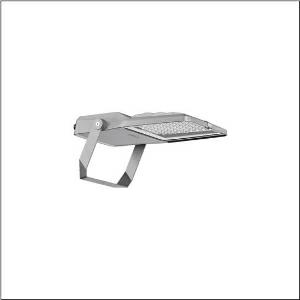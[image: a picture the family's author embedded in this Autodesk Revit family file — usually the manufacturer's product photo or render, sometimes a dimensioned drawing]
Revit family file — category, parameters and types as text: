
# Revit family: floodlight_fl_21_mini___pl64_5xa7776c4e1a_25dc
name_source: partatom
category: Lighting Fixtures
units: mm (PartAtom-declared; Revit-internal decimal feet)

## family parameters
Cut with Voids When Loaded = No
Host = Face
Light Source = No
Part Type = Normal
Room Calculation Point = No
Round Connector Dimension = Use Diameter
Shared = No

## types (1)
- --- (1 x LED, 12260 lm, 89 W, 4000K)
    Apparent Load = 89 VA
    CIE Flux Codes = 28 80 98 100 100
    Color Rendering = 70
    Color Temperature = 4000K
    Default Elevation = 1800 mm
    Description = Floodlight FL 21 mini, floodlight, primary light control with lens, of PMMA, primary optical cover: protective disc, of toughened safety glass, transparent, light distribution: PL64, light emission: direct distribution, installation type: surface-mounted, LED, High Power LED, rated luminous flux: 12.260lm, luminous efficacy: 138lm/W, light colour: 740, colour temperature: 4000K, control gear: D4iSmart Interface (Zhaga), control: overheat protection, constant luminous flux control, time-dependent luminous flux control, flexible luminous flux parameterisation, pre-setting: logarithmic dimming characteristic, with terminal, 6-pole, mains connection: 220..240V, AC, 50/60Hz, start of lifetime: 89W, end of service life: 94W, reduction: 43W, mounting bracket, of diecast aluminium, powder-coated, Siteco® metallic grey (DB 702S), corrosivity category C5 mid according to DIN EN ISO 12944, suitable for swimming pools, chlorine-resistant, sealing non-destructively replaceable, mounting bracket, of steel, galvanised, powder-coated, Siteco® metallic grey (DB 702S), Smart Interface below and above, protection rating (complete): IP66, insulation class (complete): insulation class II (safety insulation), certification: CE, ENEC, VDE, protection symbol: D, impact resistance: IK08, permissible operating ambient temperature: -40..+40°C, permissible operating ambient temperature for outdoor applications: -40..+50°C, standard: DIN EN 12944, LABS conformity tested according to VDMA 24364:2018-05, packaging unit: 1 piece

Light Distribution: PL64
    Height = 70 mm
    Lamp = 1 x LED
    Lamp Light Flux = 12260 lm
    Lamp Power = 89 W
    Lamp count = 1
    Length = 485 mm
    Luminous efficacy = 138 lm/W
    Manufacturer = Siteco
    ModVariant = No
    Model = 5XA7776C4E1A
    Number of Poles = 1
    OnlyDefault = Yes
    Power Factor = 1
    Product Name = Floodlight FL 21 mini | PL64
    Product group = floodlight | pylon annexe
    ProductGroupID = 6200
    Protection Class = Protection class II
    Protection Degree = IP 66
    RLX_Detail_Level = 1
    RLX_Emergency_Light_Flux = 0 lm
    RLX_Emergency_Type = 0
    RLX_Emergency_Type_DB = No
    RlxData = <blob elided: 95977 chars, md5=3bcb7197>
    Socket = socket
    Standby Power = 0 W
    System Light Flux = 12260 lm
    System Power = 89 W
    Type Comments = factory setting: luminous flux: 100 % | dim-lin: 254 | 456 mA
    Type Image = l_1006845.jpg
    URL = http://relux.com
    VarID = @adj_097088
    Voltage = 0 V
    Weight = 0.00 kg
    Width = 337 mm

## geometry (parser evidence)
native form markers: Blend x4, Sweep x13
no freeform markers — native parametric forms only
